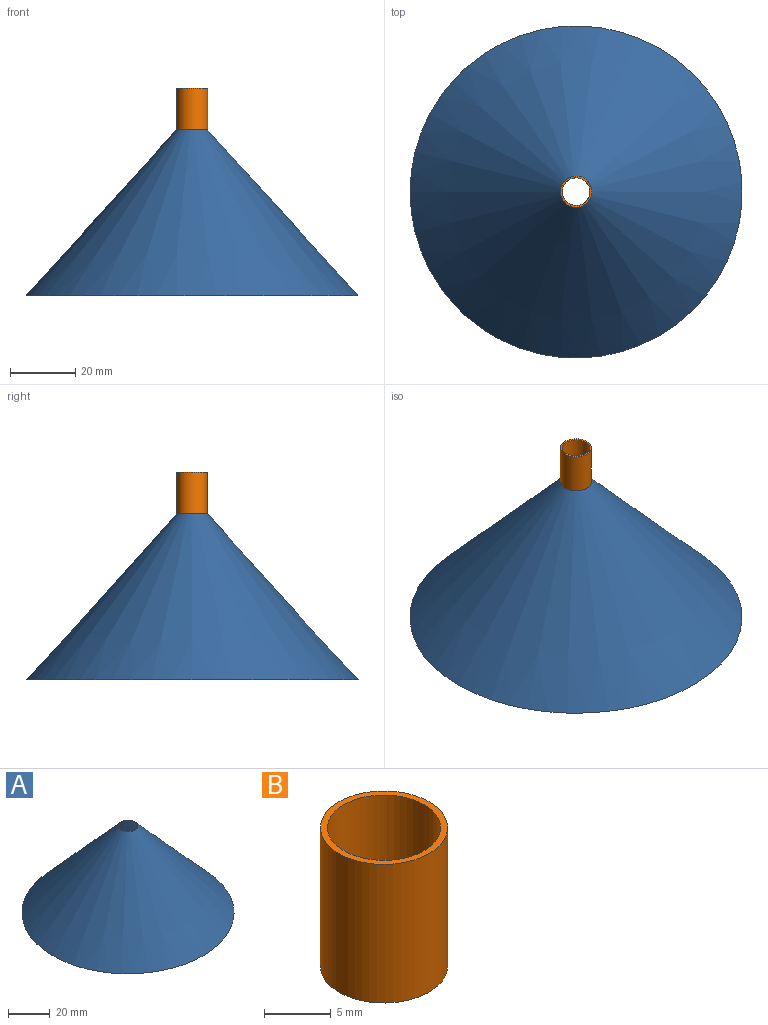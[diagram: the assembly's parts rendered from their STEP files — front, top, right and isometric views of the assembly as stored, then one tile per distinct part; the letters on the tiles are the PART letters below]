
ASSEMBLY  parts=2 mates=1
PART A: 4 faces, bbox 101.6x101.6x50.8 mm
  f0: plane 101.6x101.6mm, normal (0,0,-1), area 790.5mm2, adj f2,f3
  f1: plane 9.53x9.53mm, normal (0,0,1), area 15mm2, adj f2,f3
  f2: cone r=4.76mm half-angle=42.2deg, axis (0,0,-1), area 11967mm2, adj f0,f1
  f3: cone r=4.23mm half-angle=40.9deg, axis (0,0,-1), area 11086mm2, adj f0,f1
PART B: 4 faces, bbox 9.5x9.5x12.7 mm
  f0: cylinder r=4.76mm len=12.7mm, axis (0,0,-1), area 380mm2, adj f1,f2
  f1: plane 9.53x9.53mm, normal (0,0,1), area 15mm2, adj f0,f3
  f2: plane 9.53x9.53mm, normal (0,0,-1), area 15mm2, adj f0,f3
  f3: cylinder r=4.23mm len=12.7mm, axis (0,0,-1), area 337.8mm2, adj f1,f2
PLACE A t=(-3.82,-0.96,-23.53)mm
PLACE B t=(-3.82,-0.96,27.27)mm
MATE fastened B.f3 <-> A.f2  axis (0,0,-1) through (-3.82,-0.96,27.27)mm
